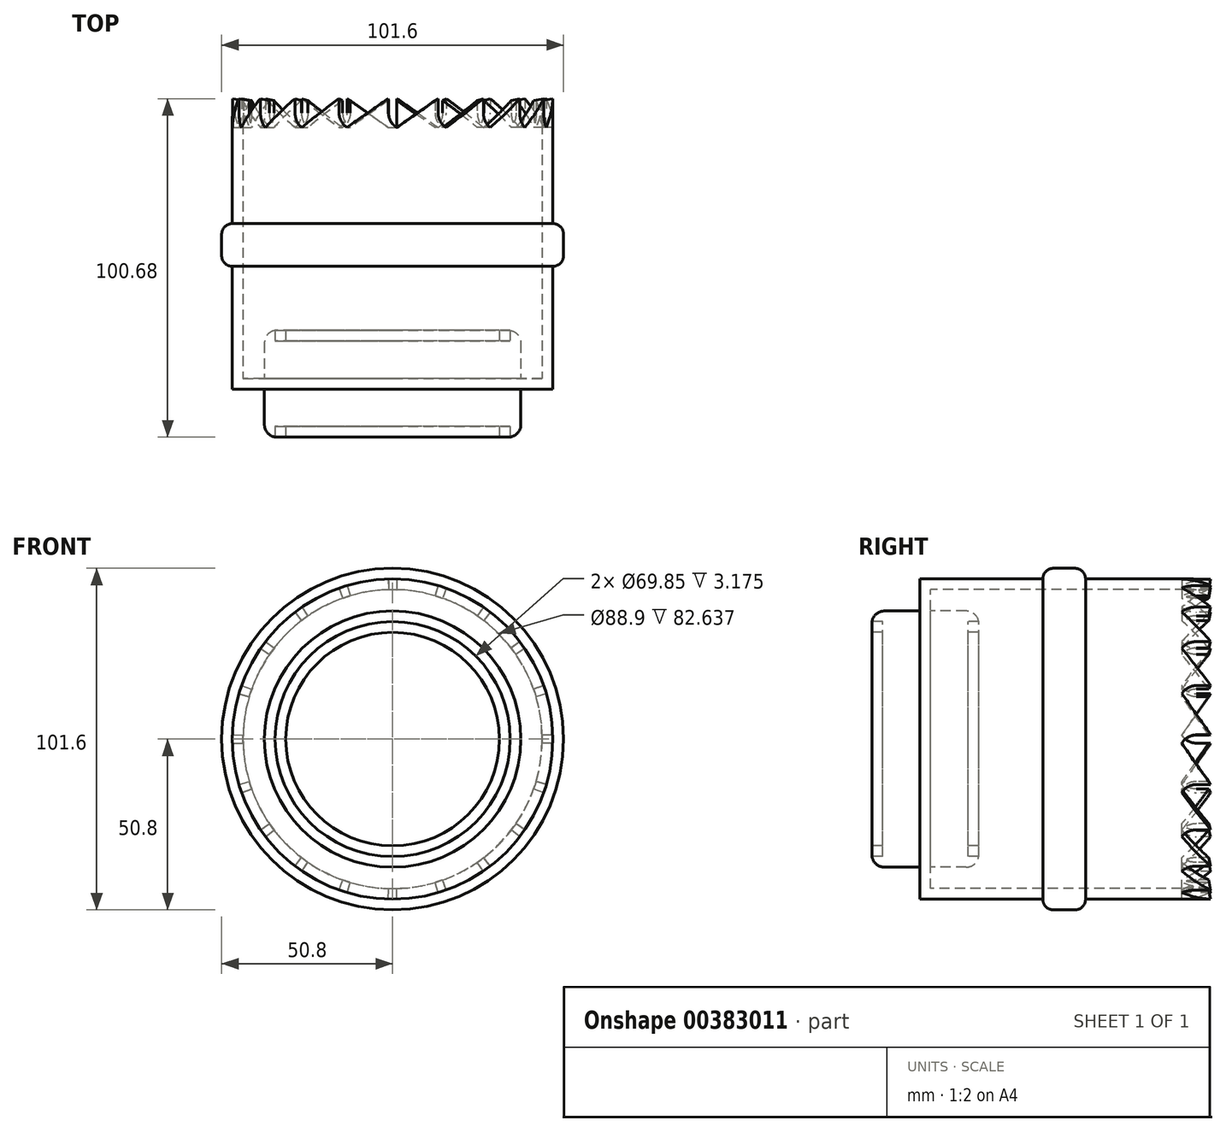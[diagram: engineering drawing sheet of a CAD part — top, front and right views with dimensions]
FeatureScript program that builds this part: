
annotation { "Feature Type Name" : "Feature", "Feature Type Description" : "" }
export const myFeature = defineFeature(function(context is Context, id is Id, definition is map)
    precondition{}
    {
        {
            var Q0;
            Q0=qCreatedBy(makeId("Front.planeOp"),FACE);
            var sketch = newSketch(context, id + "F0", { "sketchPlane" : qUnion([Q0])});
            skCircle(sketch, "E0", {"center": v(0, 0) * mm, "radius": 44.45 * mm});
            skCircle(sketch, "E1", {"center": v(0, 0) * mm, "radius": 38.1 * mm});
            skCircle(sketch, "E2", {"center": v(0, 0) * mm, "radius": 34.93 * mm});
            skCircle(sketch, "E3", {"center": v(0, 0) * mm, "radius": 31.75 * mm});
            skCircle(sketch, "E4", {"center": v(0, 0) * mm, "radius": 47.63 * mm});
            skSolve(sketch);
        }
        {
            var Q0;
            Q0=makeQuery(id+"F0.imprint","IMPRINT",FACE,{"disambiguationData":[TD([[makeQuery(id+"F0.imprint","IMPRINT",EDGE,{"derivedFrom":sQuery(id+"F0.wireOp",EDGE,"E2")}),1.0]])]});
            extrude(context, id + "F1", {"entities" : qUnion([Q0]), "endBound" : BoundingType.SYMMETRIC, "depth" : 25.4 * mm});
        }
        {
            var Q0;
            Q0=makeQuery(id+"F0.imprint","IMPRINT",FACE,{"disambiguationData":[TD([[makeQuery(id+"F0.imprint","IMPRINT",EDGE,{"derivedFrom":sQuery(id+"F0.wireOp",EDGE,"E3")}),1.0]])]});
            var Q1;
            Q1=makeQuery(id+"F0.imprint","IMPRINT",FACE,{"disambiguationData":[TD([[makeQuery(id+"F0.imprint","IMPRINT",EDGE,{"derivedFrom":sQuery(id+"F0.wireOp",EDGE,"E1")}),1.0]])]});
            extrude(context, id + "F2", {"entities" : qUnion([Q0, Q1]), "operationType" : NewBodyOperationType.ADD, "endBound" : BoundingType.SYMMETRIC, "oppositeDirection" : true, "depth" : 31.75 * mm});
        }
        {
            var Q0;
            Q0=makeQuery(id+"F0.imprint","IMPRINT",FACE,{"disambiguationData":[TD([[makeQuery(id+"F0.imprint","IMPRINT",EDGE,{"derivedFrom":sQuery(id+"F0.wireOp",EDGE,"E0")}),1.0]])]});
            extrude(context, id + "F3", {"entities" : qUnion([Q0]), "operationType" : NewBodyOperationType.ADD, "endBound" : BoundingType.SYMMETRIC, "depth" : 3.17 * mm});
        }
        {
            var Q0;
            Q0=makeQuery(id+"F0.imprint","IMPRINT",FACE,{"disambiguationData":[TD([[makeQuery(id+"F0.imprint","IMPRINT",EDGE,{"derivedFrom":sQuery(id+"F0.wireOp",EDGE,"E0")}),-1.0]])]});
            extrude(context, id + "F4", {"entities" : qUnion([Q0]), "operationType" : NewBodyOperationType.ADD, "oppositeDirection" : true, "depth" : 76.2 * mm, "hasSecondDirection" : true, "secondDirectionOppositeDirection" : false, "secondDirectionDepth" : 1.59 * mm});
        }
        {
            var Q0;
            Q0=makeQuery(id+"F2.opExtrude","CAP_EDGE",EDGE,{"disambiguationData":[OSD([sQuery(id+"F0.wireOp",EDGE,"E1")])],"isStart":false});
            var Q1;
            Q1=makeQuery(id+"F2.opExtrude","CAP_EDGE",EDGE,{"disambiguationData":[OSD([sQuery(id+"F0.wireOp",EDGE,"E1")])],"isStart":true});
            fillet(context, id + "F5", {"entities" : qUnion([Q0, Q1]), "radius" : 3.8 * mm, "tangentPropagation" : true, "allowEdgeOverflow" : false});
        }
        {
            var Q0;
            Q0=makeQuery(id+"F4.opExtrude","CAP_FACE",FACE,{"disambiguationData":[OSD([sQuery(id+"F0.wireOp",EDGE,"E0"),sQuery(id+"F0.wireOp",EDGE,"E4")])],"isStart":false});
            var sketch = newSketch(context, id + "F6", { "sketchPlane" : qUnion([Q0])});
            skCircle(sketch, "E5", {"center": v(0, 0) * mm, "radius": 47.63 * mm});
            skLineSegment(sketch, "E6", {"start": v(0, 0) * mm, "end": v(0, 47.63) * mm});
            skLineSegment(sketch, "E7", {"start": v(0, 47.63) * mm, "end": v(-1.27, 47.63) * mm});
            skLineSegment(sketch, "E8", {"start": v(0, 47.63) * mm, "end": v(1.27, 47.6) * mm});
            skLineSegment(sketch, "E9", {"start": v(1.27, 47.6) * mm, "end": v(0, 0) * mm});
            skLineSegment(sketch, "E10", {"start": v(-1.27, 47.63) * mm, "end": v(0, 0) * mm});
            skLineSegment(sketch, "E11.1.0", {"start": v(-26.96, 39.26) * mm, "end": v(0, 0) * mm});
            skLineSegment(sketch, "E11.1.1", {"start": v(-29.02, 37.78) * mm, "end": v(0, 0) * mm});
            skLineSegment(sketch, "E11.1.2", {"start": v(0, 0) * mm, "end": v(-28, 38.53) * mm});
            skLineSegment(sketch, "E11.2.0", {"start": v(-44.89, 15.92) * mm, "end": v(0, 0) * mm});
            skLineSegment(sketch, "E11.2.1", {"start": v(-45.69, 13.5) * mm, "end": v(0, 0) * mm});
            skLineSegment(sketch, "E11.2.2", {"start": v(0, 0) * mm, "end": v(-45.3, 14.72) * mm});
            skLineSegment(sketch, "E11.3.0", {"start": v(-45.67, -13.5) * mm, "end": v(0, 0) * mm});
            skLineSegment(sketch, "E11.3.1", {"start": v(-44.9, -15.92) * mm, "end": v(0, 0) * mm});
            skLineSegment(sketch, "E11.3.2", {"start": v(0, 0) * mm, "end": v(-45.3, -14.72) * mm});
            skLineSegment(sketch, "E11.4.0", {"start": v(-29.01, -37.77) * mm, "end": v(0, 0) * mm});
            skLineSegment(sketch, "E11.4.1", {"start": v(-26.97, -39.28) * mm, "end": v(0, 0) * mm});
            skLineSegment(sketch, "E11.4.2", {"start": v(0, 0) * mm, "end": v(-28, -38.53) * mm});
            skLineSegment(sketch, "E11.5.0", {"start": v(-1.27, -47.6) * mm, "end": v(0, 0) * mm});
            skLineSegment(sketch, "E11.5.1", {"start": v(1.27, -47.63) * mm, "end": v(0, 0) * mm});
            skLineSegment(sketch, "E11.5.2", {"start": v(0, 0) * mm, "end": v(0, -47.63) * mm});
            skLineSegment(sketch, "E11.6.0", {"start": v(26.96, -39.26) * mm, "end": v(0, 0) * mm});
            skLineSegment(sketch, "E11.6.1", {"start": v(29.02, -37.78) * mm, "end": v(0, 0) * mm});
            skLineSegment(sketch, "E11.6.2", {"start": v(0, 0) * mm, "end": v(28, -38.53) * mm});
            skLineSegment(sketch, "E11.7.0", {"start": v(44.89, -15.92) * mm, "end": v(0, 0) * mm});
            skLineSegment(sketch, "E11.7.1", {"start": v(45.69, -13.5) * mm, "end": v(0, 0) * mm});
            skLineSegment(sketch, "E11.7.2", {"start": v(0, 0) * mm, "end": v(45.3, -14.72) * mm});
            skLineSegment(sketch, "E11.8.0", {"start": v(45.67, 13.5) * mm, "end": v(0, 0) * mm});
            skLineSegment(sketch, "E11.8.1", {"start": v(44.9, 15.92) * mm, "end": v(0, 0) * mm});
            skLineSegment(sketch, "E11.8.2", {"start": v(0, 0) * mm, "end": v(45.3, 14.72) * mm});
            skLineSegment(sketch, "E11.9.0", {"start": v(29.01, 37.77) * mm, "end": v(0, 0) * mm});
            skLineSegment(sketch, "E11.9.1", {"start": v(26.97, 39.28) * mm, "end": v(0, 0) * mm});
            skLineSegment(sketch, "E11.9.2", {"start": v(0, 0) * mm, "end": v(28, 38.53) * mm});
            skLineSegment(sketch, "E12", {"start": v(0, 0) * mm, "end": v(47.63, 0) * mm});
            skLineSegment(sketch, "E13", {"start": v(47.63, 0) * mm, "end": v(47.63, 1.27) * mm});
            skLineSegment(sketch, "E14", {"start": v(47.63, 1.27) * mm, "end": v(0, 0) * mm});
            skLineSegment(sketch, "E15", {"start": v(47.63, 0) * mm, "end": v(47.63, -1.27) * mm});
            skLineSegment(sketch, "E16", {"start": v(47.63, -1.27) * mm, "end": v(0, 0) * mm});
            skLineSegment(sketch, "E17.1.0", {"start": v(37.78, 29.02) * mm, "end": v(0, 0) * mm});
            skLineSegment(sketch, "E17.1.1", {"start": v(39.28, 26.97) * mm, "end": v(0, 0) * mm});
            skLineSegment(sketch, "E17.1.2", {"start": v(0, 0) * mm, "end": v(38.53, 28) * mm});
            skLineSegment(sketch, "E17.2.0", {"start": v(13.5, 45.69) * mm, "end": v(0, 0) * mm});
            skLineSegment(sketch, "E17.2.1", {"start": v(15.92, 44.9) * mm, "end": v(0, 0) * mm});
            skLineSegment(sketch, "E17.2.2", {"start": v(0, 0) * mm, "end": v(14.72, 45.3) * mm});
            skLineSegment(sketch, "E17.3.0", {"start": v(-15.92, 44.9) * mm, "end": v(0, 0) * mm});
            skLineSegment(sketch, "E17.3.1", {"start": v(-13.5, 45.69) * mm, "end": v(0, 0) * mm});
            skLineSegment(sketch, "E17.3.2", {"start": v(0, 0) * mm, "end": v(-14.72, 45.3) * mm});
            skLineSegment(sketch, "E17.4.0", {"start": v(-39.28, 26.97) * mm, "end": v(0, 0) * mm});
            skLineSegment(sketch, "E17.4.1", {"start": v(-37.78, 29.02) * mm, "end": v(0, 0) * mm});
            skLineSegment(sketch, "E17.4.2", {"start": v(0, 0) * mm, "end": v(-38.53, 28) * mm});
            skLineSegment(sketch, "E17.5.0", {"start": v(-47.63, -1.27) * mm, "end": v(0, 0) * mm});
            skLineSegment(sketch, "E17.5.1", {"start": v(-47.63, 1.27) * mm, "end": v(0, 0) * mm});
            skLineSegment(sketch, "E17.5.2", {"start": v(0, 0) * mm, "end": v(-47.63, 0) * mm});
            skLineSegment(sketch, "E17.6.0", {"start": v(-37.78, -29.02) * mm, "end": v(0, 0) * mm});
            skLineSegment(sketch, "E17.6.1", {"start": v(-39.28, -26.97) * mm, "end": v(0, 0) * mm});
            skLineSegment(sketch, "E17.6.2", {"start": v(0, 0) * mm, "end": v(-38.53, -28) * mm});
            skLineSegment(sketch, "E17.7.0", {"start": v(-13.5, -45.69) * mm, "end": v(0, 0) * mm});
            skLineSegment(sketch, "E17.7.1", {"start": v(-15.92, -44.9) * mm, "end": v(0, 0) * mm});
            skLineSegment(sketch, "E17.7.2", {"start": v(0, 0) * mm, "end": v(-14.72, -45.3) * mm});
            skLineSegment(sketch, "E17.8.0", {"start": v(15.92, -44.9) * mm, "end": v(0, 0) * mm});
            skLineSegment(sketch, "E17.8.1", {"start": v(13.5, -45.69) * mm, "end": v(0, 0) * mm});
            skLineSegment(sketch, "E17.8.2", {"start": v(0, 0) * mm, "end": v(14.72, -45.3) * mm});
            skLineSegment(sketch, "E17.9.0", {"start": v(39.28, -26.97) * mm, "end": v(0, 0) * mm});
            skLineSegment(sketch, "E17.9.1", {"start": v(37.78, -29.02) * mm, "end": v(0, 0) * mm});
            skLineSegment(sketch, "E17.9.2", {"start": v(0, 0) * mm, "end": v(38.53, -28) * mm});
            skSolve(sketch);
        }
        {
            var Q0;
            {var subQ0=sQuery(id+"F6.wireOp",EDGE,"E17.4.1");var subQ1=sQuery(id+"F6.wireOp",EDGE,"E5");var subQ2=makeQuery(id+"F6.imprint","INTERSECT",VERTEX,{"derivedFrom":[subQ1,subQ0]});Q0=makeQuery(id+"F6.imprint","IMPRINT",FACE,{"disambiguationData":[TD([[makeQuery(id+"F6.imprint","IMPRINT",EDGE,{"disambiguationData":[TD([[subQ2,-1.0]])],"derivedFrom":subQ1}),-1.0]])]});}
            var Q1;
            {var subQ0=sQuery(id+"F6.wireOp",EDGE,"E11.1.0");var subQ1=sQuery(id+"F6.wireOp",EDGE,"E5");var subQ2=makeQuery(id+"F6.imprint","INTERSECT",VERTEX,{"derivedFrom":[subQ1,subQ0]});Q1=makeQuery(id+"F6.imprint","IMPRINT",FACE,{"disambiguationData":[TD([[makeQuery(id+"F6.imprint","IMPRINT",EDGE,{"disambiguationData":[TD([[subQ2,-1.0]])],"derivedFrom":subQ1}),-1.0]])]});}
            var Q2;
            {var subQ0=sQuery(id+"F6.wireOp",EDGE,"E17.3.1");var subQ1=sQuery(id+"F6.wireOp",EDGE,"E5");var subQ2=makeQuery(id+"F6.imprint","INTERSECT",VERTEX,{"derivedFrom":[subQ1,subQ0]});Q2=makeQuery(id+"F6.imprint","IMPRINT",FACE,{"disambiguationData":[TD([[makeQuery(id+"F6.imprint","IMPRINT",EDGE,{"disambiguationData":[TD([[subQ2,-1.0]])],"derivedFrom":subQ1}),-1.0]])]});}
            var Q3;
            {var subQ1=sQuery(id+"F6.wireOp",EDGE,"E5");var subQ3=sQuery(id+"F6.wireOp",EDGE,"E17.2.0");var subQ4=makeQuery(id+"F6.imprint","INTERSECT",VERTEX,{"derivedFrom":[subQ1,subQ3]});Q3=makeQuery(id+"F6.imprint","IMPRINT",FACE,{"disambiguationData":[TD([[makeQuery(id+"F6.imprint","IMPRINT",EDGE,{"disambiguationData":[TD([[subQ4,-1.0]])],"derivedFrom":subQ3}),-1.0]])]});}
            var Q4;
            {var subQ0=sQuery(id+"F6.wireOp",EDGE,"E17.2.1");var subQ1=sQuery(id+"F6.wireOp",EDGE,"E5");var subQ2=makeQuery(id+"F6.imprint","INTERSECT",VERTEX,{"derivedFrom":[subQ1,subQ0]});Q4=makeQuery(id+"F6.imprint","IMPRINT",FACE,{"disambiguationData":[TD([[makeQuery(id+"F6.imprint","IMPRINT",EDGE,{"disambiguationData":[TD([[subQ2,-1.0]])],"derivedFrom":subQ1}),-1.0]])]});}
            var Q5;
            {var subQ0=sQuery(id+"F6.wireOp",EDGE,"E11.9.0");var subQ1=sQuery(id+"F6.wireOp",EDGE,"E5");var subQ2=makeQuery(id+"F6.imprint","INTERSECT",VERTEX,{"derivedFrom":[subQ1,subQ0]});Q5=makeQuery(id+"F6.imprint","IMPRINT",FACE,{"disambiguationData":[TD([[makeQuery(id+"F6.imprint","IMPRINT",EDGE,{"disambiguationData":[TD([[subQ2,-1.0]])],"derivedFrom":subQ1}),-1.0]])]});}
            var Q6;
            {var subQ0=sQuery(id+"F6.wireOp",EDGE,"E17.1.1");var subQ1=sQuery(id+"F6.wireOp",EDGE,"E5");var subQ2=makeQuery(id+"F6.imprint","INTERSECT",VERTEX,{"derivedFrom":[subQ1,subQ0]});Q6=makeQuery(id+"F6.imprint","IMPRINT",FACE,{"disambiguationData":[TD([[makeQuery(id+"F6.imprint","IMPRINT",EDGE,{"disambiguationData":[TD([[subQ2,-1.0]])],"derivedFrom":subQ1}),-1.0]])]});}
            var Q7;
            {var subQ0=sQuery(id+"F6.wireOp",EDGE,"E11.8.0");var subQ1=sQuery(id+"F6.wireOp",EDGE,"E5");var subQ2=makeQuery(id+"F6.imprint","INTERSECT",VERTEX,{"derivedFrom":[subQ1,subQ0]});Q7=makeQuery(id+"F6.imprint","IMPRINT",FACE,{"disambiguationData":[TD([[makeQuery(id+"F6.imprint","IMPRINT",EDGE,{"disambiguationData":[TD([[subQ2,-1.0]])],"derivedFrom":subQ1}),-1.0]])]});}
            var Q8;
            {var subQ0=sQuery(id+"F6.wireOp",EDGE,"E11.7.1");var subQ1=sQuery(id+"F6.wireOp",EDGE,"E5");var subQ2=makeQuery(id+"F6.imprint","INTERSECT",VERTEX,{"derivedFrom":[subQ1,subQ0]});Q8=makeQuery(id+"F6.imprint","IMPRINT",FACE,{"disambiguationData":[TD([[makeQuery(id+"F6.imprint","IMPRINT",EDGE,{"disambiguationData":[TD([[subQ2,1.0]])],"derivedFrom":subQ1}),-1.0]])]});}
            var Q9;
            {var subQ0=sQuery(id+"F6.wireOp",EDGE,"E11.7.0");var subQ1=sQuery(id+"F6.wireOp",EDGE,"E5");var subQ2=makeQuery(id+"F6.imprint","INTERSECT",VERTEX,{"derivedFrom":[subQ1,subQ0]});Q9=makeQuery(id+"F6.imprint","IMPRINT",FACE,{"disambiguationData":[TD([[makeQuery(id+"F6.imprint","IMPRINT",EDGE,{"disambiguationData":[TD([[subQ2,-1.0]])],"derivedFrom":subQ1}),-1.0]])]});}
            var Q10;
            {var subQ0=sQuery(id+"F6.wireOp",EDGE,"E17.9.1");var subQ1=sQuery(id+"F6.wireOp",EDGE,"E5");var subQ2=makeQuery(id+"F6.imprint","INTERSECT",VERTEX,{"derivedFrom":[subQ1,subQ0]});Q10=makeQuery(id+"F6.imprint","IMPRINT",FACE,{"disambiguationData":[TD([[makeQuery(id+"F6.imprint","IMPRINT",EDGE,{"disambiguationData":[TD([[subQ2,-1.0]])],"derivedFrom":subQ1}),-1.0]])]});}
            var Q11;
            {var subQ0=sQuery(id+"F6.wireOp",EDGE,"E11.6.0");var subQ1=sQuery(id+"F6.wireOp",EDGE,"E5");var subQ2=makeQuery(id+"F6.imprint","INTERSECT",VERTEX,{"derivedFrom":[subQ1,subQ0]});Q11=makeQuery(id+"F6.imprint","IMPRINT",FACE,{"disambiguationData":[TD([[makeQuery(id+"F6.imprint","IMPRINT",EDGE,{"disambiguationData":[TD([[subQ2,-1.0]])],"derivedFrom":subQ1}),-1.0]])]});}
            var Q12;
            {var subQ0=sQuery(id+"F6.wireOp",EDGE,"E17.8.1");var subQ1=sQuery(id+"F6.wireOp",EDGE,"E5");var subQ2=makeQuery(id+"F6.imprint","INTERSECT",VERTEX,{"derivedFrom":[subQ1,subQ0]});Q12=makeQuery(id+"F6.imprint","IMPRINT",FACE,{"disambiguationData":[TD([[makeQuery(id+"F6.imprint","IMPRINT",EDGE,{"disambiguationData":[TD([[subQ2,-1.0]])],"derivedFrom":subQ1}),-1.0]])]});}
            var Q13;
            {var subQ0=sQuery(id+"F6.wireOp",EDGE,"E11.5.0");var subQ1=sQuery(id+"F6.wireOp",EDGE,"E5");var subQ2=makeQuery(id+"F6.imprint","INTERSECT",VERTEX,{"derivedFrom":[subQ1,subQ0]});Q13=makeQuery(id+"F6.imprint","IMPRINT",FACE,{"disambiguationData":[TD([[makeQuery(id+"F6.imprint","IMPRINT",EDGE,{"disambiguationData":[TD([[subQ2,-1.0]])],"derivedFrom":subQ1}),-1.0]])]});}
            var Q14;
            {var subQ0=sQuery(id+"F6.wireOp",EDGE,"E17.7.1");var subQ1=sQuery(id+"F6.wireOp",EDGE,"E5");var subQ2=makeQuery(id+"F6.imprint","INTERSECT",VERTEX,{"derivedFrom":[subQ1,subQ0]});Q14=makeQuery(id+"F6.imprint","IMPRINT",FACE,{"disambiguationData":[TD([[makeQuery(id+"F6.imprint","IMPRINT",EDGE,{"disambiguationData":[TD([[subQ2,-1.0]])],"derivedFrom":subQ1}),-1.0]])]});}
            var Q15;
            {var subQ0=sQuery(id+"F6.wireOp",EDGE,"E11.4.0");var subQ1=sQuery(id+"F6.wireOp",EDGE,"E5");var subQ2=makeQuery(id+"F6.imprint","INTERSECT",VERTEX,{"derivedFrom":[subQ1,subQ0]});Q15=makeQuery(id+"F6.imprint","IMPRINT",FACE,{"disambiguationData":[TD([[makeQuery(id+"F6.imprint","IMPRINT",EDGE,{"disambiguationData":[TD([[subQ2,-1.0]])],"derivedFrom":subQ1}),-1.0]])]});}
            var Q16;
            {var subQ0=sQuery(id+"F6.wireOp",EDGE,"E17.6.1");var subQ1=sQuery(id+"F6.wireOp",EDGE,"E5");var subQ2=makeQuery(id+"F6.imprint","INTERSECT",VERTEX,{"derivedFrom":[subQ1,subQ0]});Q16=makeQuery(id+"F6.imprint","IMPRINT",FACE,{"disambiguationData":[TD([[makeQuery(id+"F6.imprint","IMPRINT",EDGE,{"disambiguationData":[TD([[subQ2,-1.0]])],"derivedFrom":subQ1}),-1.0]])]});}
            var Q17;
            {var subQ0=sQuery(id+"F6.wireOp",EDGE,"E11.2.0");var subQ1=sQuery(id+"F6.wireOp",EDGE,"E5");var subQ2=makeQuery(id+"F6.imprint","INTERSECT",VERTEX,{"derivedFrom":[subQ1,subQ0]});Q17=makeQuery(id+"F6.imprint","IMPRINT",FACE,{"disambiguationData":[TD([[makeQuery(id+"F6.imprint","IMPRINT",EDGE,{"disambiguationData":[TD([[subQ2,-1.0]])],"derivedFrom":subQ1}),-1.0]])]});}
            var Q18;
            {var subQ0=sQuery(id+"F6.wireOp",EDGE,"E11.3.0");var subQ1=sQuery(id+"F6.wireOp",EDGE,"E5");var subQ2=makeQuery(id+"F6.imprint","INTERSECT",VERTEX,{"derivedFrom":[subQ1,subQ0]});Q18=makeQuery(id+"F6.imprint","IMPRINT",FACE,{"disambiguationData":[TD([[makeQuery(id+"F6.imprint","IMPRINT",EDGE,{"disambiguationData":[TD([[subQ2,-1.0]])],"derivedFrom":subQ1}),-1.0]])]});}
            var Q19;
            {var subQ0=sQuery(id+"F6.wireOp",EDGE,"E17.5.1");var subQ1=sQuery(id+"F6.wireOp",EDGE,"E5");var subQ2=makeQuery(id+"F6.imprint","INTERSECT",VERTEX,{"derivedFrom":[subQ1,subQ0]});Q19=makeQuery(id+"F6.imprint","IMPRINT",FACE,{"disambiguationData":[TD([[makeQuery(id+"F6.imprint","IMPRINT",EDGE,{"disambiguationData":[TD([[subQ2,-1.0]])],"derivedFrom":subQ1}),-1.0]])]});}
            extrude(context, id + "F7", {"entities" : qUnion([Q0, Q1, Q2, Q3, Q4, Q5, Q6, Q7, Q8, Q9, Q10, Q11, Q12, Q13, Q14, Q15, Q16, Q17, Q18, Q19]), "operationType" : NewBodyOperationType.ADD, "depth" : 8.9 * mm});
        }
        {
            var Q0;
            Q0=makeQuery(id+"F7.opExtrude","CAP_EDGE",EDGE,{"disambiguationData":[OSD([sQuery(id+"F6.wireOp",EDGE,"E17.5.1")])],"isStart":true});
            var Q1;
            Q1=makeQuery(id+"F7.opExtrude","CAP_EDGE",EDGE,{"disambiguationData":[OSD([sQuery(id+"F6.wireOp",EDGE,"E11.2.0")])],"isStart":true});
            var Q2;
            Q2=makeQuery(id+"F7.opExtrude","CAP_EDGE",EDGE,{"disambiguationData":[OSD([sQuery(id+"F6.wireOp",EDGE,"E11.3.0")])],"isStart":true});
            var Q3;
            Q3=makeQuery(id+"F7.opExtrude","CAP_EDGE",EDGE,{"disambiguationData":[OSD([sQuery(id+"F6.wireOp",EDGE,"E17.4.1")])],"isStart":true});
            var Q4;
            Q4=makeQuery(id+"F7.opExtrude","CAP_EDGE",EDGE,{"disambiguationData":[OSD([sQuery(id+"F6.wireOp",EDGE,"E11.1.0")])],"isStart":true});
            var Q5;
            Q5=makeQuery(id+"F7.opExtrude","CAP_EDGE",EDGE,{"disambiguationData":[OSD([sQuery(id+"F6.wireOp",EDGE,"E17.6.1")])],"isStart":true});
            var Q6;
            Q6=makeQuery(id+"F7.opExtrude","CAP_EDGE",EDGE,{"disambiguationData":[OSD([sQuery(id+"F6.wireOp",EDGE,"E11.4.0")])],"isStart":true});
            var Q7;
            Q7=makeQuery(id+"F7.opExtrude","CAP_EDGE",EDGE,{"disambiguationData":[OSD([sQuery(id+"F6.wireOp",EDGE,"E17.7.1")])],"isStart":true});
            var Q8;
            Q8=makeQuery(id+"F7.opExtrude","CAP_EDGE",EDGE,{"disambiguationData":[OSD([sQuery(id+"F6.wireOp",EDGE,"E11.5.0")])],"isStart":true});
            var Q9;
            Q9=makeQuery(id+"F7.opExtrude","CAP_EDGE",EDGE,{"disambiguationData":[OSD([sQuery(id+"F6.wireOp",EDGE,"E17.8.1")])],"isStart":true});
            var Q10;
            Q10=makeQuery(id+"F7.opExtrude","CAP_EDGE",EDGE,{"disambiguationData":[OSD([sQuery(id+"F6.wireOp",EDGE,"E11.6.0")])],"isStart":true});
            var Q11;
            Q11=makeQuery(id+"F7.opExtrude","CAP_EDGE",EDGE,{"disambiguationData":[OSD([sQuery(id+"F6.wireOp",EDGE,"E17.9.1")])],"isStart":true});
            var Q12;
            Q12=makeQuery(id+"F7.opExtrude","CAP_EDGE",EDGE,{"disambiguationData":[OSD([sQuery(id+"F6.wireOp",EDGE,"E11.7.0")])],"isStart":true});
            var Q13;
            Q13=makeQuery(id+"F7.opExtrude","CAP_EDGE",EDGE,{"disambiguationData":[OSD([sQuery(id+"F6.wireOp",EDGE,"E16")])],"isStart":true});
            var Q14;
            Q14=makeQuery(id+"F7.opExtrude","CAP_EDGE",EDGE,{"disambiguationData":[OSD([sQuery(id+"F6.wireOp",EDGE,"E11.8.0")])],"isStart":true});
            var Q15;
            Q15=makeQuery(id+"F7.opExtrude","CAP_EDGE",EDGE,{"disambiguationData":[OSD([sQuery(id+"F6.wireOp",EDGE,"E17.1.1")])],"isStart":true});
            var Q16;
            Q16=makeQuery(id+"F7.opExtrude","CAP_EDGE",EDGE,{"disambiguationData":[OSD([sQuery(id+"F6.wireOp",EDGE,"E11.9.0")])],"isStart":true});
            var Q17;
            Q17=makeQuery(id+"F7.opExtrude","CAP_EDGE",EDGE,{"disambiguationData":[OSD([sQuery(id+"F6.wireOp",EDGE,"E17.2.1")])],"isStart":true});
            var Q18;
            Q18=makeQuery(id+"F7.opExtrude","CAP_EDGE",EDGE,{"disambiguationData":[OSD([sQuery(id+"F6.wireOp",EDGE,"E9")])],"isStart":true});
            var Q19;
            Q19=makeQuery(id+"F7.opExtrude","CAP_EDGE",EDGE,{"disambiguationData":[OSD([sQuery(id+"F6.wireOp",EDGE,"E17.3.1")])],"isStart":true});
            fillet(context, id + "F8", {"entities" : qUnion([Q0, Q1, Q2, Q3, Q4, Q5, Q6, Q7, Q8, Q9, Q10, Q11, Q12, Q13, Q14, Q15, Q16, Q17, Q18, Q19]), "radius" : 5.08 * mm, "tangentPropagation" : true, "allowEdgeOverflow" : false});
        }
        {
            var Q0;
            Q0=makeQuery(id+"F7.opExtrude","CAP_EDGE",EDGE,{"disambiguationData":[OSD([sQuery(id+"F6.wireOp",EDGE,"E11.1.1")])],"isStart":false});
            var Q1;
            Q1=makeQuery(id+"F7.opExtrude","CAP_EDGE",EDGE,{"disambiguationData":[OSD([sQuery(id+"F6.wireOp",EDGE,"E17.4.0")])],"isStart":false});
            var Q2;
            Q2=makeQuery(id+"F7.opExtrude","CAP_EDGE",EDGE,{"disambiguationData":[OSD([sQuery(id+"F6.wireOp",EDGE,"E11.2.1")])],"isStart":false});
            var Q3;
            Q3=makeQuery(id+"F7.opExtrude","CAP_EDGE",EDGE,{"disambiguationData":[OSD([sQuery(id+"F6.wireOp",EDGE,"E17.5.0")])],"isStart":false});
            var Q4;
            Q4=makeQuery(id+"F7.opExtrude","CAP_EDGE",EDGE,{"disambiguationData":[OSD([sQuery(id+"F6.wireOp",EDGE,"E11.3.1")])],"isStart":false});
            var Q5;
            Q5=makeQuery(id+"F7.opExtrude","CAP_EDGE",EDGE,{"disambiguationData":[OSD([sQuery(id+"F6.wireOp",EDGE,"E17.6.0")])],"isStart":false});
            var Q6;
            Q6=makeQuery(id+"F7.opExtrude","CAP_EDGE",EDGE,{"disambiguationData":[OSD([sQuery(id+"F6.wireOp",EDGE,"E11.4.1")])],"isStart":false});
            var Q7;
            Q7=makeQuery(id+"F7.opExtrude","CAP_EDGE",EDGE,{"disambiguationData":[OSD([sQuery(id+"F6.wireOp",EDGE,"E17.7.0")])],"isStart":false});
            var Q8;
            Q8=makeQuery(id+"F7.opExtrude","CAP_EDGE",EDGE,{"disambiguationData":[OSD([sQuery(id+"F6.wireOp",EDGE,"E11.5.1")])],"isStart":false});
            var Q9;
            Q9=makeQuery(id+"F7.opExtrude","CAP_EDGE",EDGE,{"disambiguationData":[OSD([sQuery(id+"F6.wireOp",EDGE,"E17.8.0")])],"isStart":false});
            var Q10;
            Q10=makeQuery(id+"F7.opExtrude","CAP_EDGE",EDGE,{"disambiguationData":[OSD([sQuery(id+"F6.wireOp",EDGE,"E11.6.1")])],"isStart":false});
            var Q11;
            Q11=makeQuery(id+"F7.opExtrude","CAP_EDGE",EDGE,{"disambiguationData":[OSD([sQuery(id+"F6.wireOp",EDGE,"E17.9.0")])],"isStart":false});
            var Q12;
            Q12=makeQuery(id+"F7.opExtrude","CAP_EDGE",EDGE,{"disambiguationData":[OSD([sQuery(id+"F6.wireOp",EDGE,"E11.7.1")])],"isStart":false});
            var Q13;
            Q13=makeQuery(id+"F7.opExtrude","CAP_EDGE",EDGE,{"disambiguationData":[OSD([sQuery(id+"F6.wireOp",EDGE,"E14")])],"isStart":false});
            var Q14;
            Q14=makeQuery(id+"F7.opExtrude","CAP_EDGE",EDGE,{"disambiguationData":[OSD([sQuery(id+"F6.wireOp",EDGE,"E11.8.1")])],"isStart":false});
            var Q15;
            Q15=makeQuery(id+"F7.opExtrude","CAP_EDGE",EDGE,{"disambiguationData":[OSD([sQuery(id+"F6.wireOp",EDGE,"E17.1.0")])],"isStart":false});
            var Q16;
            Q16=makeQuery(id+"F7.opExtrude","CAP_EDGE",EDGE,{"disambiguationData":[OSD([sQuery(id+"F6.wireOp",EDGE,"E11.9.1")])],"isStart":false});
            var Q17;
            Q17=makeQuery(id+"F7.opExtrude","CAP_EDGE",EDGE,{"disambiguationData":[OSD([sQuery(id+"F6.wireOp",EDGE,"E17.2.0")])],"isStart":false});
            var Q18;
            Q18=makeQuery(id+"F7.opExtrude","CAP_EDGE",EDGE,{"disambiguationData":[OSD([sQuery(id+"F6.wireOp",EDGE,"E10")])],"isStart":false});
            var Q19;
            Q19=makeQuery(id+"F7.opExtrude","CAP_EDGE",EDGE,{"disambiguationData":[OSD([sQuery(id+"F6.wireOp",EDGE,"E17.3.0")])],"isStart":false});
            chamfer(context, id + "F9", {"entities" : qUnion([Q0, Q1, Q2, Q3, Q4, Q5, Q6, Q7, Q8, Q9, Q10, Q11, Q12, Q13, Q14, Q15, Q16, Q17, Q18, Q19]), "chamferType" : ChamferType.TWO_OFFSETS, "width1" : 8.9 * mm, "oppositeDirection" : false, "width2" : 12.7 * mm, "tangentPropagation" : true});
        }
        {
            var Q0;
            Q0=makeQuery(id+"F2.opExtrude","CAP_FACE",FACE,{"disambiguationData":[OSD([sQuery(id+"F0.wireOp",EDGE,"E3")])],"isStart":false});
            cPlane(context, id + "F10", {"entities" : qUnion([Q0]), "cplaneType" : CPlaneType.OFFSET, "offset" : 25.4 * mm, "width" : 152.4 * mm, "height" : 152.4 * mm});
        }
        {
            var Q0;
            Q0=qCreatedBy(id+"F10.planeOp",FACE);
            var sketch = newSketch(context, id + "F11", { "sketchPlane" : qUnion([Q0])});
            skCircle(sketch, "E18.0.0", {"center": v(0, 0) * mm, "radius": 44.45 * mm});
            skCircle(sketch, "E19", {"center": v(0, 0) * mm, "radius": 47.63 * mm});
            skCircle(sketch, "E20.0", {"center": v(0, 0) * mm, "radius": 50.8 * mm});
            skLineSegment(sketch, "E21", {"start": v(0, 0) * mm, "end": v(6.35, 0) * mm});
            skLineSegment(sketch, "E22", {"start": v(0, 0) * mm, "end": v(-6.35, 0) * mm});
            skLineSegment(sketch, "E23", {"start": v(0, 0) * mm, "end": v(-6.35, 50.4) * mm});
            skLineSegment(sketch, "E24", {"start": v(0, 0) * mm, "end": v(6.35, 50.4) * mm});
            skLineSegment(sketch, "E25.1.0", {"start": v(1.39, 2.4) * mm, "end": v(-45.44, -17.3) * mm});
            skLineSegment(sketch, "E25.1.1", {"start": v(1.39, 2.4) * mm, "end": v(-39.09, -28.3) * mm});
            skLineSegment(sketch, "E25.2.0", {"start": v(-1.39, 2.4) * mm, "end": v(39.09, -28.3) * mm});
            skLineSegment(sketch, "E25.2.1", {"start": v(-1.39, 2.4) * mm, "end": v(45.44, -17.3) * mm});
            skPoint(sketch, "E25.center", {"position": v(0, 1.6) * mm});
            skLineSegment(sketch, "E26", {"start": v(0, 0) * mm, "end": v(-3.18, 0) * mm});
            skLineSegment(sketch, "E27", {"start": v(-3.18, 0) * mm, "end": v(-1.59, 0) * mm});
            skLineSegment(sketch, "E28", {"start": v(0, 0) * mm, "end": v(3.18, 0) * mm});
            skLineSegment(sketch, "E29", {"start": v(3.18, 0) * mm, "end": v(1.59, 0) * mm});
            skLineSegment(sketch, "E30", {"start": v(0, 0) * mm, "end": v(-3.18, 50.7) * mm});
            skLineSegment(sketch, "E31", {"start": v(0, 0) * mm, "end": v(3.17, 50.7) * mm});
            skLineSegment(sketch, "E32", {"start": v(0, 0) * mm, "end": v(1.59, 50.78) * mm});
            skPoint(sketch, "E32.endSnap0", {"position": v(1.59, 25.35) * mm});
            skLineSegment(sketch, "E33", {"start": v(0, 0) * mm, "end": v(-1.59, 50.78) * mm});
            skLineSegment(sketch, "E34.1.0", {"start": v(1.39, 2.4) * mm, "end": v(-40.93, -25.7) * mm});
            skLineSegment(sketch, "E34.1.1", {"start": v(1.39, 2.4) * mm, "end": v(-41.8, -24.37) * mm});
            skLineSegment(sketch, "E34.1.2", {"start": v(1.39, 2.4) * mm, "end": v(-43.38, -21.62) * mm});
            skLineSegment(sketch, "E34.1.3", {"start": v(1.39, 2.4) * mm, "end": v(-44.1, -20.2) * mm});
            skLineSegment(sketch, "E34.2.0", {"start": v(-1.38, 2.4) * mm, "end": v(44.12, -20.2) * mm});
            skLineSegment(sketch, "E34.2.1", {"start": v(-1.38, 2.4) * mm, "end": v(43.39, -21.62) * mm});
            skLineSegment(sketch, "E34.2.2", {"start": v(-1.38, 2.4) * mm, "end": v(41.8, -24.37) * mm});
            skLineSegment(sketch, "E34.2.3", {"start": v(-1.38, 2.4) * mm, "end": v(40.94, -25.7) * mm});
            skSolve(sketch);
        }
        {
            var Q0;
            {var subQ0=sQuery(id+"F11.wireOp",EDGE,"E30");var subQ1=sQuery(id+"F11.wireOp",EDGE,"E19");var subQ2=makeQuery(id+"F11.imprint","INTERSECT",VERTEX,{"derivedFrom":[subQ1,subQ0]});Q0=makeQuery(id+"F11.imprint","IMPRINT",FACE,{"disambiguationData":[TD([[makeQuery(id+"F11.imprint","IMPRINT",EDGE,{"disambiguationData":[TD([[subQ2,-1.0]])],"derivedFrom":subQ1}),-1.0]])]});}
            var Q1;
            {var subQ0=sQuery(id+"F11.wireOp",EDGE,"E32");var subQ1=sQuery(id+"F11.wireOp",EDGE,"E19");var subQ2=makeQuery(id+"F11.imprint","INTERSECT",VERTEX,{"derivedFrom":[subQ1,subQ0]});Q1=makeQuery(id+"F11.imprint","IMPRINT",FACE,{"disambiguationData":[TD([[makeQuery(id+"F11.imprint","IMPRINT",EDGE,{"disambiguationData":[TD([[subQ2,-1.0]])],"derivedFrom":subQ1}),-1.0]])]});}
            var Q2;
            {var subQ0=sQuery(id+"F11.wireOp",EDGE,"E31");var subQ1=sQuery(id+"F11.wireOp",EDGE,"E19");var subQ2=makeQuery(id+"F11.imprint","INTERSECT",VERTEX,{"derivedFrom":[subQ1,subQ0]});Q2=makeQuery(id+"F11.imprint","IMPRINT",FACE,{"disambiguationData":[TD([[makeQuery(id+"F11.imprint","IMPRINT",EDGE,{"disambiguationData":[TD([[subQ2,1.0]])],"derivedFrom":subQ1}),-1.0]])]});}
            var Q3;
            {var subQ0=sQuery(id+"F11.wireOp",EDGE,"E34.2.0");var subQ1=sQuery(id+"F11.wireOp",EDGE,"E19");var subQ2=makeQuery(id+"F11.imprint","INTERSECT",VERTEX,{"derivedFrom":[subQ1,subQ0]});Q3=makeQuery(id+"F11.imprint","IMPRINT",FACE,{"disambiguationData":[TD([[makeQuery(id+"F11.imprint","IMPRINT",EDGE,{"disambiguationData":[TD([[subQ2,-1.0]])],"derivedFrom":subQ1}),-1.0]])]});}
            var Q4;
            {var subQ0=sQuery(id+"F11.wireOp",EDGE,"E34.2.2");var subQ1=sQuery(id+"F11.wireOp",EDGE,"E19");var subQ2=makeQuery(id+"F11.imprint","INTERSECT",VERTEX,{"derivedFrom":[subQ1,subQ0]});Q4=makeQuery(id+"F11.imprint","IMPRINT",FACE,{"disambiguationData":[TD([[makeQuery(id+"F11.imprint","IMPRINT",EDGE,{"disambiguationData":[TD([[subQ2,-1.0]])],"derivedFrom":subQ1}),-1.0]])]});}
            var Q5;
            {var subQ0=sQuery(id+"F11.wireOp",EDGE,"E25.2.0");var subQ1=sQuery(id+"F11.wireOp",EDGE,"E19");var subQ2=makeQuery(id+"F11.imprint","INTERSECT",VERTEX,{"derivedFrom":[subQ1,subQ0]});Q5=makeQuery(id+"F11.imprint","IMPRINT",FACE,{"disambiguationData":[TD([[makeQuery(id+"F11.imprint","IMPRINT",EDGE,{"disambiguationData":[TD([[subQ2,-1.0]])],"derivedFrom":subQ1}),-1.0]])]});}
            var Q6;
            {var subQ0=sQuery(id+"F11.wireOp",EDGE,"E31");var subQ1=sQuery(id+"F11.wireOp",EDGE,"E19");var subQ2=makeQuery(id+"F11.imprint","INTERSECT",VERTEX,{"derivedFrom":[subQ1,subQ0]});Q6=makeQuery(id+"F11.imprint","IMPRINT",FACE,{"disambiguationData":[TD([[makeQuery(id+"F11.imprint","IMPRINT",EDGE,{"disambiguationData":[TD([[subQ2,-1.0]])],"derivedFrom":subQ1}),-1.0]])]});}
            var Q7;
            {var subQ0=sQuery(id+"F11.wireOp",EDGE,"E33");var subQ1=sQuery(id+"F11.wireOp",EDGE,"E19");var subQ2=makeQuery(id+"F11.imprint","INTERSECT",VERTEX,{"derivedFrom":[subQ1,subQ0]});Q7=makeQuery(id+"F11.imprint","IMPRINT",FACE,{"disambiguationData":[TD([[makeQuery(id+"F11.imprint","IMPRINT",EDGE,{"disambiguationData":[TD([[subQ2,-1.0]])],"derivedFrom":subQ1}),-1.0]])]});}
            var Q8;
            {var subQ0=sQuery(id+"F11.wireOp",EDGE,"E34.1.0");var subQ1=sQuery(id+"F11.wireOp",EDGE,"E19");var subQ2=makeQuery(id+"F11.imprint","INTERSECT",VERTEX,{"derivedFrom":[subQ1,subQ0]});Q8=makeQuery(id+"F11.imprint","IMPRINT",FACE,{"disambiguationData":[TD([[makeQuery(id+"F11.imprint","IMPRINT",EDGE,{"disambiguationData":[TD([[subQ2,-1.0]])],"derivedFrom":subQ1}),-1.0]])]});}
            var Q9;
            {var subQ0=sQuery(id+"F11.wireOp",EDGE,"E34.1.1");var subQ1=sQuery(id+"F11.wireOp",EDGE,"E19");var subQ2=makeQuery(id+"F11.imprint","INTERSECT",VERTEX,{"derivedFrom":[subQ1,subQ0]});Q9=makeQuery(id+"F11.imprint","IMPRINT",FACE,{"disambiguationData":[TD([[makeQuery(id+"F11.imprint","IMPRINT",EDGE,{"disambiguationData":[TD([[subQ2,-1.0]])],"derivedFrom":subQ1}),-1.0]])]});}
            var Q10;
            {var subQ0=sQuery(id+"F11.wireOp",EDGE,"E34.1.2");var subQ1=sQuery(id+"F11.wireOp",EDGE,"E19");var subQ2=makeQuery(id+"F11.imprint","INTERSECT",VERTEX,{"derivedFrom":[subQ1,subQ0]});Q10=makeQuery(id+"F11.imprint","IMPRINT",FACE,{"disambiguationData":[TD([[makeQuery(id+"F11.imprint","IMPRINT",EDGE,{"disambiguationData":[TD([[subQ2,-1.0]])],"derivedFrom":subQ1}),-1.0]])]});}
            var Q11;
            {var subQ0=sQuery(id+"F11.wireOp",EDGE,"E34.1.3");var subQ1=sQuery(id+"F11.wireOp",EDGE,"E19");var subQ2=makeQuery(id+"F11.imprint","INTERSECT",VERTEX,{"derivedFrom":[subQ1,subQ0]});Q11=makeQuery(id+"F11.imprint","IMPRINT",FACE,{"disambiguationData":[TD([[makeQuery(id+"F11.imprint","IMPRINT",EDGE,{"disambiguationData":[TD([[subQ2,-1.0]])],"derivedFrom":subQ1}),-1.0]])]});}
            var Q12;
            {var subQ0=sQuery(id+"F11.wireOp",EDGE,"E25.1.0");var subQ1=sQuery(id+"F11.wireOp",EDGE,"E19");var subQ2=makeQuery(id+"F11.imprint","INTERSECT",VERTEX,{"derivedFrom":[subQ1,subQ0]});Q12=makeQuery(id+"F11.imprint","IMPRINT",FACE,{"disambiguationData":[TD([[makeQuery(id+"F11.imprint","IMPRINT",EDGE,{"disambiguationData":[TD([[subQ2,-1.0]])],"derivedFrom":subQ1}),-1.0]])]});}
            var Q13;
            {var subQ0=sQuery(id+"F11.wireOp",EDGE,"E34.2.3");var subQ1=sQuery(id+"F11.wireOp",EDGE,"E19");var subQ2=makeQuery(id+"F11.imprint","INTERSECT",VERTEX,{"derivedFrom":[subQ1,subQ0]});Q13=makeQuery(id+"F11.imprint","IMPRINT",FACE,{"disambiguationData":[TD([[makeQuery(id+"F11.imprint","IMPRINT",EDGE,{"disambiguationData":[TD([[subQ2,-1.0]])],"derivedFrom":subQ1}),-1.0]])]});}
            var Q14;
            {var subQ0=sQuery(id+"F11.wireOp",EDGE,"E34.2.1");var subQ1=sQuery(id+"F11.wireOp",EDGE,"E19");var subQ2=makeQuery(id+"F11.imprint","INTERSECT",VERTEX,{"derivedFrom":[subQ1,subQ0]});Q14=makeQuery(id+"F11.imprint","IMPRINT",FACE,{"disambiguationData":[TD([[makeQuery(id+"F11.imprint","IMPRINT",EDGE,{"disambiguationData":[TD([[subQ2,-1.0]])],"derivedFrom":subQ1}),-1.0]])]});}
            var Q15;
            {var subQ0=sQuery(id+"F11.wireOp",EDGE,"E24");var subQ1=sQuery(id+"F11.wireOp",EDGE,"E19");var subQ2=makeQuery(id+"F11.imprint","INTERSECT",VERTEX,{"derivedFrom":[subQ1,subQ0]});Q15=makeQuery(id+"F11.imprint","IMPRINT",FACE,{"disambiguationData":[TD([[makeQuery(id+"F11.imprint","IMPRINT",EDGE,{"disambiguationData":[TD([[subQ2,1.0]])],"derivedFrom":subQ1}),-1.0]])]});}
            var Q16;
            {var subQ0=sQuery(id+"F11.wireOp",EDGE,"E23");var subQ1=sQuery(id+"F11.wireOp",EDGE,"E19");var subQ2=makeQuery(id+"F11.imprint","INTERSECT",VERTEX,{"derivedFrom":[subQ1,subQ0]});Q16=makeQuery(id+"F11.imprint","IMPRINT",FACE,{"disambiguationData":[TD([[makeQuery(id+"F11.imprint","IMPRINT",EDGE,{"disambiguationData":[TD([[subQ2,-1.0]])],"derivedFrom":subQ1}),-1.0]])]});}
            var Q17;
            {var subQ0=sQuery(id+"F11.wireOp",EDGE,"E25.1.1");var subQ1=sQuery(id+"F11.wireOp",EDGE,"E19");var subQ2=makeQuery(id+"F11.imprint","INTERSECT",VERTEX,{"derivedFrom":[subQ1,subQ0]});Q17=makeQuery(id+"F11.imprint","IMPRINT",FACE,{"disambiguationData":[TD([[makeQuery(id+"F11.imprint","IMPRINT",EDGE,{"disambiguationData":[TD([[subQ2,-1.0]])],"derivedFrom":subQ1}),-1.0]])]});}
            extrude(context, id + "F12", {"entities" : qUnion([Q0, Q1, Q2, Q3, Q4, Q5, Q6, Q7, Q8, Q9, Q10, Q11, Q12, Q13, Q14, Q15, Q16, Q17]), "operationType" : NewBodyOperationType.ADD, "endBound" : BoundingType.SYMMETRIC, "depth" : 12.7 * mm});
        }
        {
            var Q0;
            Q0=makeQuery(id+"F12.opExtrude","CAP_EDGE",EDGE,{"disambiguationData":[OSD([sQuery(id+"F11.wireOp",EDGE,"E20.0")])],"isStart":false});
            var Q1;
            Q1=makeQuery(id+"F12.opExtrude","CAP_EDGE",EDGE,{"disambiguationData":[OSD([sQuery(id+"F11.wireOp",EDGE,"E20.0")])],"isStart":true});
            fillet(context, id + "F13", {"entities" : qUnion([Q0, Q1]), "radius" : 3.17 * mm, "tangentPropagation" : true, "allowEdgeOverflow" : false});
        }
    });
